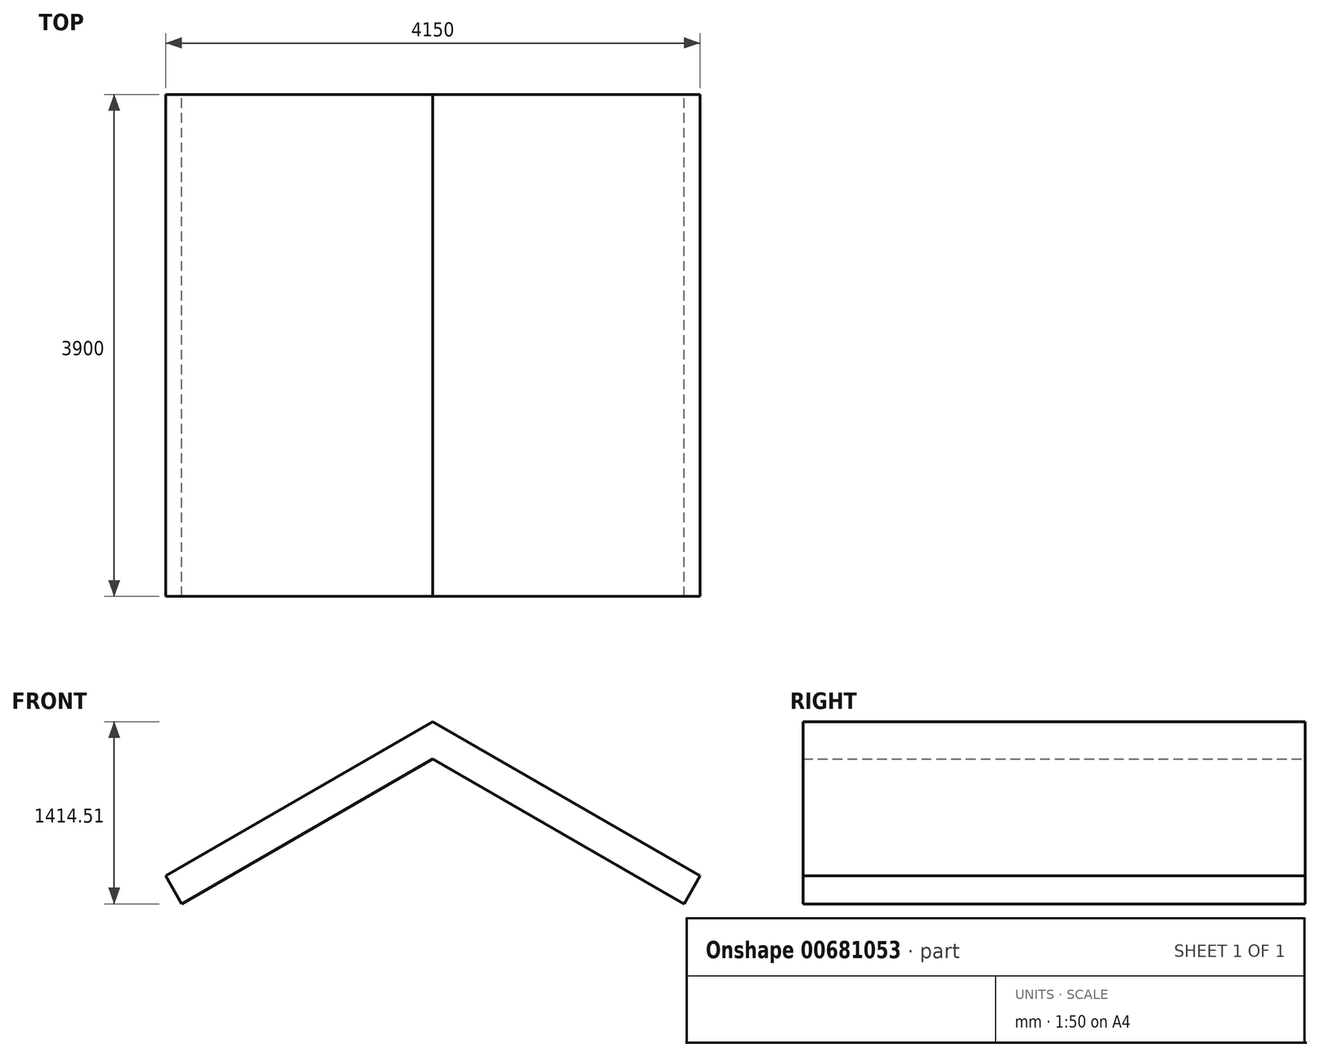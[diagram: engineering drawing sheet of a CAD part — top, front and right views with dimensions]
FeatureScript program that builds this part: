
annotation { "Feature Type Name" : "Feature", "Feature Type Description" : "" }
export const myFeature = defineFeature(function(context is Context, id is Id, definition is map)
    precondition{}
    {
        {
            var Q0;
            Q0=qCreatedBy(makeId("Front.planeOp"),FACE);
            var sketch = newSketch(context, id + "F0", { "sketchPlane" : qUnion([Q0])});
            skLineSegment(sketch, "E0", {"start": v(-1950, 0) * mm, "end": v(-2075, 216.5) * mm});
            skLineSegment(sketch, "E1", {"start": v(-2075, 216.5) * mm, "end": v(0, 1414.5) * mm});
            skLineSegment(sketch, "E2", {"start": v(0, 1414.5) * mm, "end": v(2075, 216.5) * mm});
            skLineSegment(sketch, "E3", {"start": v(2075, 216.5) * mm, "end": v(1950, 0) * mm});
            skLineSegment(sketch, "E4", {"start": v(1950, 0) * mm, "end": v(0, 1125.83) * mm});
            skLineSegment(sketch, "E5", {"start": v(0, 1125.83) * mm, "end": v(-1950, 0) * mm});
            skLineSegment(sketch, "E6", {"start": v(0, 0) * mm, "end": v(0, 1414.5) * mm, "construction": true});
            skLineSegment(sketch, "E7", {"start": v(-1950, 0) * mm, "end": v(1950, 0) * mm, "construction": true});
            skSolve(sketch);
        }
        {
            var Q0;
            Q0 = qSketchRegion(id + "F0", true);
            extrude(context, id + "F1", {"entities" : qUnion([Q0]), "depth" : 3900 * mm, "offsetDistance" : 25 * mm});
        }
    });
